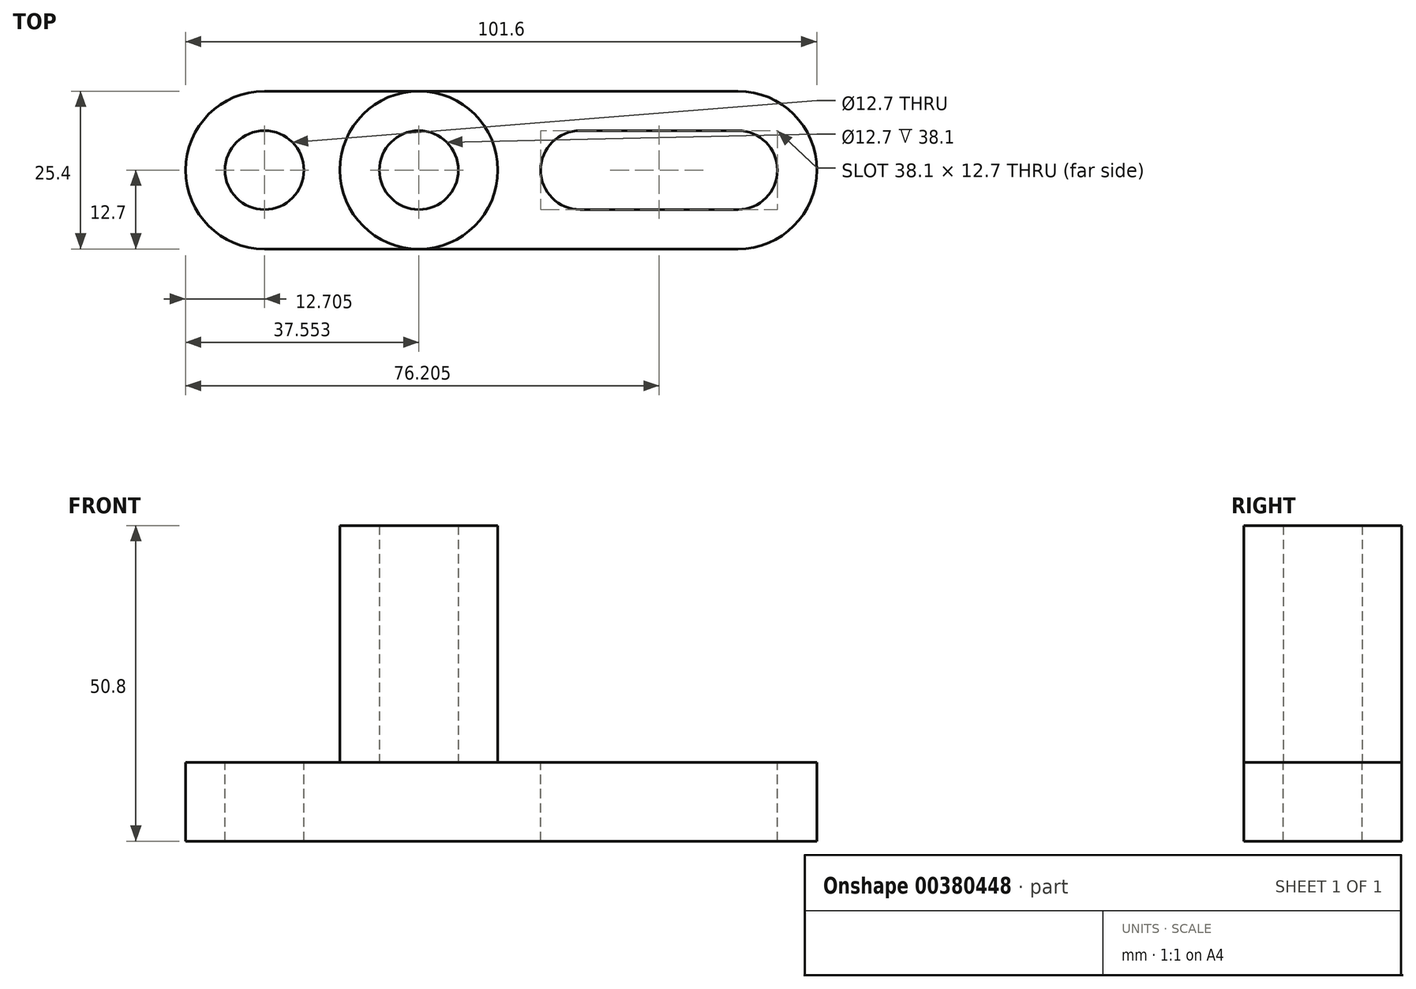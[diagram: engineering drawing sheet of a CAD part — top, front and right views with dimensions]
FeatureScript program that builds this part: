
annotation { "Feature Type Name" : "Feature", "Feature Type Description" : "" }
export const myFeature = defineFeature(function(context is Context, id is Id, definition is map)
    precondition{}
    {
        {
            var Q0;
            Q0=qCreatedBy(makeId("Top.planeOp"),FACE);
            var sketch = newSketch(context, id + "F0", { "sketchPlane" : qUnion([Q0])});
            skLineSegment(sketch, "E0.bottom", {"start": v(-33.22, 0) * mm, "end": v(68.38, 0) * mm});
            skLineSegment(sketch, "E0.top", {"start": v(-33.22, 25.4) * mm, "end": v(68.38, 25.4) * mm});
            skLineSegment(sketch, "E0.left", {"start": v(-33.22, 0) * mm, "end": v(-33.22, 25.4) * mm});
            skLineSegment(sketch, "E0.right", {"start": v(68.38, 0) * mm, "end": v(68.38, 25.4) * mm});
            skSolve(sketch);
        }
        {
            var Q0;
            Q0=makeQuery(id+"F0.imprint","IMPRINT",FACE,{"disambiguationData":[TD([[makeQuery(id+"F0.imprint","IMPRINT",EDGE,{"derivedFrom":sQuery(id+"F0.wireOp",EDGE,"E0.bottom")}),1.0]])]});
            extrude(context, id + "F1", {"entities" : qUnion([Q0]), "oppositeDirection" : true, "depth" : 12.7 * mm});
        }
        {
            var Q0;
            Q0=makeQuery(id+"F1.opExtrude","CAP_FACE",FACE,{"disambiguationData":[OSD([sQuery(id+"F0.wireOp",EDGE,"E0.bottom"),sQuery(id+"F0.wireOp",EDGE,"E0.top"),sQuery(id+"F0.wireOp",EDGE,"E0.left"),sQuery(id+"F0.wireOp",EDGE,"E0.right")])],"isStart":true});
            var sketch = newSketch(context, id + "F2", { "sketchPlane" : qUnion([Q0])});
            skArc(sketch, "E1", {"start": v(-20.52, 25.4) * mm, "mid": v(-33.22, 12.7) * mm, "end": v(-20.52, 0) * mm});
            skArc(sketch, "E2", {"start": v(55.68, 0) * mm, "mid": v(68.38, 12.7) * mm, "end": v(55.68, 25.4) * mm});
            skCircle(sketch, "E3", {"center": v(55.68, 12.7) * mm, "radius": 6.35 * mm});
            skCircle(sketch, "E4", {"center": v(30.28, 12.7) * mm, "radius": 6.35 * mm});
            skLineSegment(sketch, "E5", {"start": v(30.28, 19.05) * mm, "end": v(55.68, 19.05) * mm});
            skLineSegment(sketch, "E6", {"start": v(30.28, 6.35) * mm, "end": v(55.68, 6.35) * mm});
            skCircle(sketch, "E7", {"center": v(-20.52, 12.7) * mm, "radius": 6.35 * mm});
            skSolve(sketch);
        }
        {
            var Q0;
            {var subQ0=sQuery(id+"F2.wireOp",EDGE,"E3");var subQ1=makeQuery(id+"F2.imprint","INTERSECT",VERTEX,{"derivedFrom":[subQ0,sQuery(id+"F2.wireOp",EDGE,"E5")]});Q0=makeQuery(id+"F2.imprint","IMPRINT",FACE,{"disambiguationData":[TD([[makeQuery(id+"F2.imprint","IMPRINT",EDGE,{"disambiguationData":[TD([[subQ1,-1.0]])],"derivedFrom":subQ0}),1.0]])]});}
            var Q1;
            {var subQ0=sQuery(id+"F2.wireOp",EDGE,"E4");var subQ1=makeQuery(id+"F2.imprint","INTERSECT",VERTEX,{"derivedFrom":[subQ0,sQuery(id+"F2.wireOp",EDGE,"E5")]});Q1=makeQuery(id+"F2.imprint","IMPRINT",FACE,{"disambiguationData":[TD([[makeQuery(id+"F2.imprint","IMPRINT",EDGE,{"disambiguationData":[TD([[subQ1,-1.0]])],"derivedFrom":subQ0}),1.0]])]});}
            var Q2;
            {var subQ0=sQuery(id+"F2.wireOp",EDGE,"E1");var subQ1=makeQuery(id+"F1.opExtrude","CAP_EDGE",EDGE,{"disambiguationData":[OSD([sQuery(id+"F0.wireOp",EDGE,"E0.top")])],"isStart":true});var subQ2=makeQuery(id+"F2.imprint","INTERSECT",VERTEX,{"derivedFrom":[subQ1,subQ0]});Q2=makeQuery(id+"F2.imprint","IMPRINT",FACE,{"disambiguationData":[TD([[makeQuery(id+"F2.imprint","IMPRINT",EDGE,{"disambiguationData":[TD([[subQ2,-1.0]])],"derivedFrom":subQ0}),-1.0]])]});}
            var Q3;
            {var subQ0=sQuery(id+"F2.wireOp",EDGE,"E1");var subQ1=makeQuery(id+"F1.opExtrude","CAP_EDGE",EDGE,{"disambiguationData":[OSD([sQuery(id+"F0.wireOp",EDGE,"E0.bottom")])],"isStart":true});var subQ2=makeQuery(id+"F2.imprint","INTERSECT",VERTEX,{"derivedFrom":[subQ1,subQ0]});Q3=makeQuery(id+"F2.imprint","IMPRINT",FACE,{"disambiguationData":[TD([[makeQuery(id+"F2.imprint","IMPRINT",EDGE,{"disambiguationData":[TD([[subQ2,1.0]])],"derivedFrom":subQ0}),-1.0]])]});}
            var Q4;
            {var subQ0=sQuery(id+"F2.wireOp",EDGE,"E2");var subQ1=makeQuery(id+"F1.opExtrude","CAP_EDGE",EDGE,{"disambiguationData":[OSD([sQuery(id+"F0.wireOp",EDGE,"E0.top")])],"isStart":true});var subQ2=makeQuery(id+"F2.imprint","INTERSECT",VERTEX,{"derivedFrom":[subQ1,subQ0]});Q4=makeQuery(id+"F2.imprint","IMPRINT",FACE,{"disambiguationData":[TD([[makeQuery(id+"F2.imprint","IMPRINT",EDGE,{"disambiguationData":[TD([[subQ2,1.0]])],"derivedFrom":subQ0}),-1.0]])]});}
            var Q5;
            {var subQ0=sQuery(id+"F2.wireOp",EDGE,"E2");var subQ1=makeQuery(id+"F1.opExtrude","CAP_EDGE",EDGE,{"disambiguationData":[OSD([sQuery(id+"F0.wireOp",EDGE,"E0.bottom")])],"isStart":true});var subQ2=makeQuery(id+"F2.imprint","INTERSECT",VERTEX,{"derivedFrom":[subQ1,subQ0]});Q5=makeQuery(id+"F2.imprint","IMPRINT",FACE,{"disambiguationData":[TD([[makeQuery(id+"F2.imprint","IMPRINT",EDGE,{"disambiguationData":[TD([[subQ2,-1.0]])],"derivedFrom":subQ0}),-1.0]])]});}
            var Q6;
            {var subQ0=sQuery(id+"F2.wireOp",EDGE,"E5");Q6=makeQuery(id+"F2.imprint","IMPRINT",FACE,{"disambiguationData":[TD([[makeQuery(id+"F2.imprint","IMPRINT",EDGE,{"derivedFrom":subQ0}),-1.0]])]});}
            var Q7;
            Q7=makeQuery(id+"F2.imprint","IMPRINT",FACE,{"disambiguationData":[TD([[makeQuery(id+"F2.imprint","IMPRINT",EDGE,{"derivedFrom":sQuery(id+"F2.wireOp",EDGE,"E7")}),1.0]])]});
            extrude(context, id + "F3", {"entities" : qUnion([Q0, Q1, Q2, Q3, Q4, Q5, Q6, Q7]), "operationType" : NewBodyOperationType.REMOVE, "oppositeDirection" : true, "depth" : 25.4 * mm});
        }
        {
            var Q0;
            Q0=makeQuery(id+"F1.opExtrude","CAP_FACE",FACE,{"disambiguationData":[OSD([sQuery(id+"F0.wireOp",EDGE,"E0.bottom"),sQuery(id+"F0.wireOp",EDGE,"E0.top"),sQuery(id+"F0.wireOp",EDGE,"E0.left"),sQuery(id+"F0.wireOp",EDGE,"E0.right")])],"isStart":true});
            var sketch = newSketch(context, id + "F4", { "sketchPlane" : qUnion([Q0])});
            skCircle(sketch, "E8", {"center": v(4.33, 12.7) * mm, "radius": 12.7 * mm});
            skCircle(sketch, "E9", {"center": v(4.33, 12.7) * mm, "radius": 6.35 * mm});
            skSolve(sketch);
        }
        {
            var Q0;
            Q0=makeQuery(id+"F4.imprint","IMPRINT",FACE,{"disambiguationData":[TD([[makeQuery(id+"F4.imprint","IMPRINT",EDGE,{"derivedFrom":sQuery(id+"F4.wireOp",EDGE,"E9")}),-1.0]])]});
            extrude(context, id + "F5", {"entities" : qUnion([Q0]), "operationType" : NewBodyOperationType.ADD, "depth" : 38.1 * mm});
        }
    });
